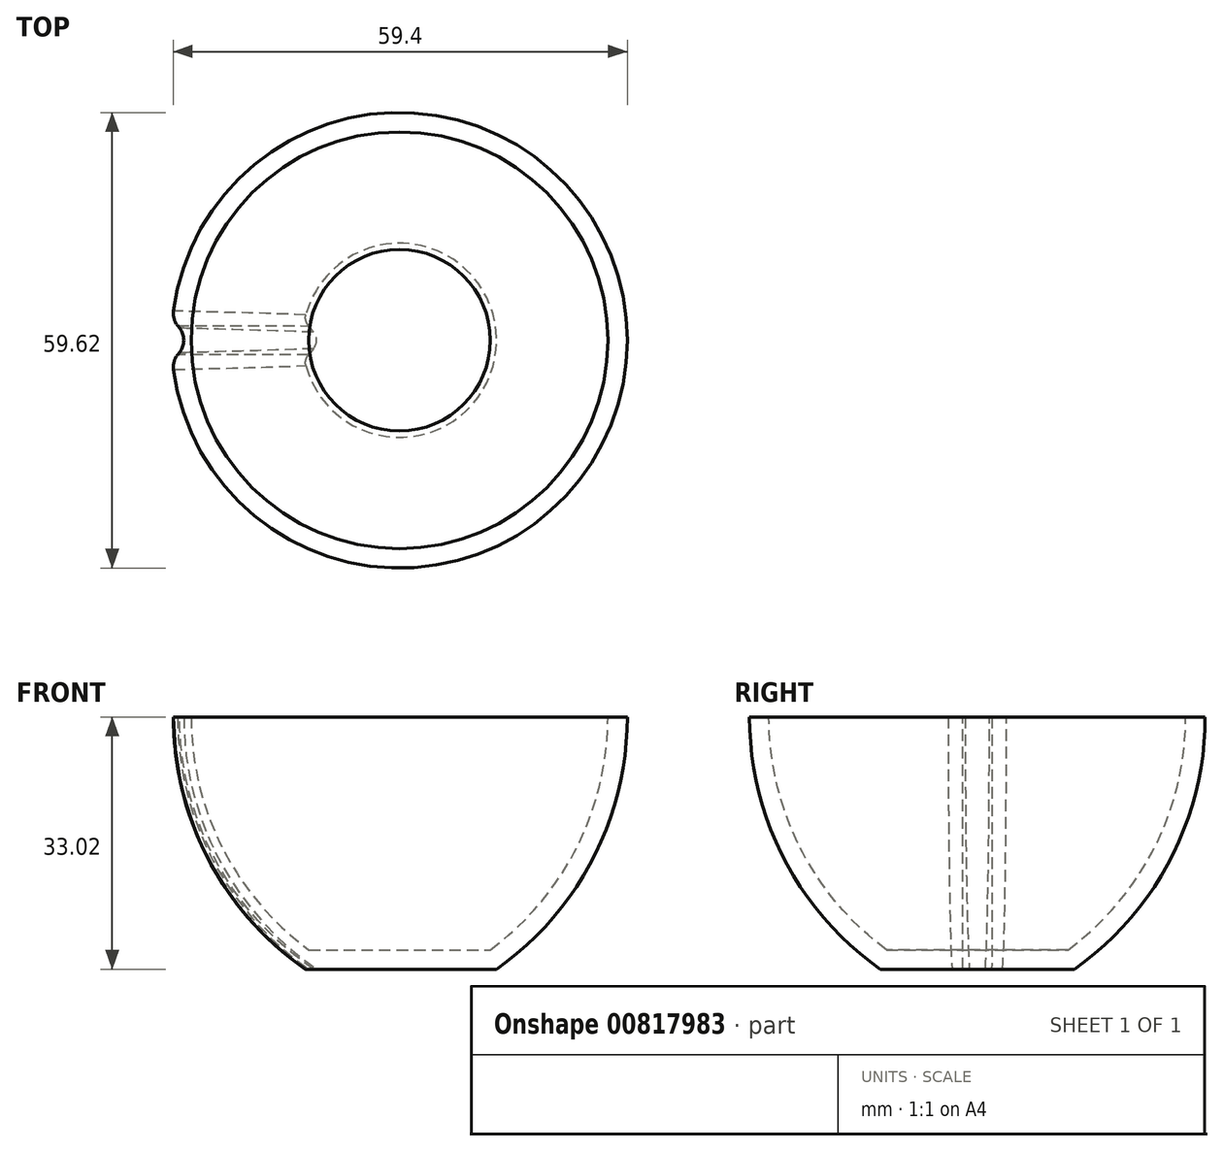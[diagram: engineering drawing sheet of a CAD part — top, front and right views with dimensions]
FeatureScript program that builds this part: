
annotation { "Feature Type Name" : "Feature", "Feature Type Description" : "" }
export const myFeature = defineFeature(function(context is Context, id is Id, definition is map)
    precondition{}
    {
        {
            var Q0;
            Q0=qCreatedBy(makeId("Front.planeOp"),FACE);
            var sketch = newSketch(context, id + "F0", { "sketchPlane" : qUnion([Q0])});
            skLineSegment(sketch, "E0", {"start": v(-12.7, 0) * mm, "end": v(0, 0) * mm});
            skArc(sketch, "E1", {"start": v(-29.81, 33.02) * mm, "mid": v(-25.28, 14.42) * mm, "end": v(-12.7, 0) * mm});
            skLineSegment(sketch, "E2", {"start": v(-29.81, 33.02) * mm, "end": v(0, 33.02) * mm});
            skLineSegment(sketch, "E3", {"start": v(0, 33.02) * mm, "end": v(0, 0) * mm});
            skSolve(sketch);
        }
        {
            var Q0;
            Q0 = qSketchRegion(id + "F0", true);
            var Q1;
            Q1=sQuery(id+"F0.wireOp",EDGE,"E3");
            revolve(context, id + "F1", {"surfaceOperationType" : NewSurfaceOperationType.NEW, "entities" : qUnion([Q0]), "axis" : qUnion([Q1]), "revolveType" : RevolveType.FULL});
        }
        {
            var Q0;
            Q0=makeQuery(id+"F1.opRevolve","SWEPT_FACE",FACE,{"disambiguationData":[OSD([sQuery(id+"F0.wireOp",EDGE,"E2")])]});
            shell(context, id + "F2", {"entities" : qUnion([Q0]), "thickness" : 2.54 * mm});
        }
        {
            var Q0;
            Q0=qCreatedBy(makeId("Top.planeOp"),FACE);
            var sketch = newSketch(context, id + "F3", { "sketchPlane" : qUnion([Q0])});
            skCircle(sketch, "E4", {"center": v(0, 0) * mm, "radius": 12.95 * mm});
            skPoint(sketch, "E5.visualSharp", {"position": v(-10.41, 0) * mm});
            skLineSegment(sketch, "E6", {"start": v(-10.41, 0) * mm, "end": v(-12.64, -2.81) * mm});
            skLineSegment(sketch, "E7.MirrorCS", {"start": v(-10.41, 0) * mm, "end": v(-12.64, 2.81) * mm});
            skSolve(sketch);
        }
        {
            var Q0;
            {var subQ0=sQuery(id+"F3.wireOp",EDGE,"E6");Q0=makeQuery(id+"F3.imprint","IMPRINT",FACE,{"disambiguationData":[TD([[makeQuery(id+"F3.imprint","IMPRINT",EDGE,{"derivedFrom":subQ0}),-1.0]])]});}
            var Q1;
            Q1=sQuery(id+"F0.wireOp",EDGE,"E1");
            sweep(context, id + "F4", {"operationType" : NewBodyOperationType.REMOVE, "profiles" : qUnion([Q0]), "path" : qUnion([Q1]), "keepProfileOrientation" : true});
        }
        {
            var Q0;
            {var subQ0=sQuery(id+"F0.wireOp",EDGE,"E1");Q0=makeQuery(id+"F4.boolean.opBoolean","INTERSECT",EDGE,{"derivedFrom":[makeQuery(id+"F1.opRevolve","SWEPT_FACE",FACE,{"disambiguationData":[OSD([subQ0])]}),makeQuery(id+"F4.opSweep","SWEPT_FACE",FACE,{"disambiguationData":[OSD([subQ0,sQuery(id+"F3.wireOp",EDGE,"E7.MirrorCS")])]})]});}
            var Q1;
            Q1=makeQuery(id+"F4.boolean.opBoolean","COPY",EDGE,{"derivedFrom":makeQuery(id+"F4.opSweep","SWEPT_EDGE",EDGE,{"disambiguationData":[OSD([sQuery(id+"F0.wireOp",EDGE,"E1"),sQuery(id+"F3.wireOp",EDGE,"E6"),sQuery(id+"F3.wireOp",EDGE,"E7.MirrorCS")])]})});
            var Q2;
            {var subQ0=sQuery(id+"F0.wireOp",EDGE,"E1");Q2=makeQuery(id+"F4.boolean.opBoolean","INTERSECT",EDGE,{"derivedFrom":[makeQuery(id+"F1.opRevolve","SWEPT_FACE",FACE,{"disambiguationData":[OSD([subQ0])]}),makeQuery(id+"F4.opSweep","SWEPT_FACE",FACE,{"disambiguationData":[OSD([subQ0,sQuery(id+"F3.wireOp",EDGE,"E6")])]})]});}
            fillet(context, id + "F5", {"entities" : qUnion([Q0, Q1, Q2]), "radius" : 2.54 * mm, "tangentPropagation" : true, "allowEdgeOverflow" : false});
        }
    });
